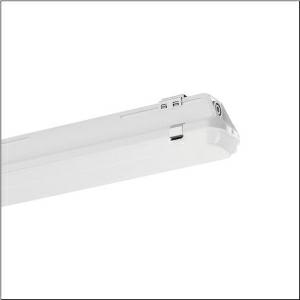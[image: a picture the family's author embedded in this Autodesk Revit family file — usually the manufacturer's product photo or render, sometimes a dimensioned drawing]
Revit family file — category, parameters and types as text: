
# Revit family: monsun_r__11_51fp208p460h_1e38
name_source: partatom
category: Lighting Fixtures
units: mm (PartAtom-declared; Revit-internal decimal feet)

## family parameters
Cut with Voids When Loaded = No
Host = Face
Light Source = No
Part Type = Normal
Room Calculation Point = No
Round Connector Dimension = Use Diameter
Shared = No

## types (1)
- Monsun® 11 (1 x LED, 5490 lm, 33.9 W, 4000K)
    Apparent Load = 34 VA
    CIE Flux Codes = 45 75 93 94 100
    Color Rendering = 80
    Color Temperature = 4000K
    Default Elevation = 1800 mm
    Description = Monsun® 11, damp-proof luminaire, chain hanger, primary optical cover: enclosure, of PC, light emission: direct distribution, primary light characteristic: symmetric, installation type: suspended mounting, surface-mounted, horizontal mounting, vertical mounting, LED, rated luminous flux: 5.490lm, luminous efficacy: 162lm/W, light colour: 840, colour temperature: 4000K, control gear: ON/OFF, with terminal, 3-pole, max. 2.5mm², mains connection: 220..240V, AC, 50/60Hz, rated input power: 34W, luminaire housing, of glass-fibre reinforced polyester, uncoated, bright grey, incl. chain hanger, length: 1.590mm, width: 90mm, height: 88mm, clip for enclosure, of stainless steel (V2A), ceiling mounting element, of stainless steel (V2A), chain hanger, of stainless steel (V2A), protection rating (complete): IP66, insulation class (complete): insulation class I (protective earthing), certification: CE, ENEC, VDE, UKCA, protection symbol: D, impact resistance: IK08, permissible operating ambient temperature: -35..+40°C, standard: EN 50419, EN 60598-2-1, no direct snow, no direct sun, no direct rain, for indoor or canopied outdoor use, corresponds to IFS (International Featured Standards) requirements for safety and quality in the food industry, contact your sales advisor before using the luminaires in applications with unclear chemical exposure, large temperature fluctuations or condensation-forming humidity, LABS conformity tested according to VDMA 24364:2018-05, packaging unit: 1 piece
    Height = 89 mm
    Lamp = 1 x LED
    Lamp Light Flux = 5490 lm
    Lamp Power = 33.9 W
    Lamp count = 1
    Length = 1590 mm
    Luminous efficacy = 162 lm/W
    Manufacturer = Siteco
    ModVariant = No
    Model = 51FP208P460H
    Mounting Place = Ceiling
    Mounting Type = Surface mounted
    Number of Poles = 1
    OnlyDefault = Yes
    Power Factor = 1
    Product Name = Monsun® 11
    Product group = damp-proof luminaire
    ProductGroupID = 300
    Protection Class = Protection class I
    Protection Degree = IP 66
    RLX_Detail_Level = 1
    RLX_Emergency_Light_Flux = 0 lm
    RLX_Emergency_Type = 0
    RLX_Emergency_Type_DB = No
    RlxData = <blob elided: 88741 chars, md5=bf3f0788>
    Socket = socket
    Standby Power = 0 W
    System Light Flux = 5490 lm
    System Power = 34 W
    Type Comments = Product without accessories
    Type Image = l_1349237.jpg
    URL = http://relux.com
    VarID = ---
    Voltage = 0 V
    Weight = 0.00 kg
    Width = 90 mm

## geometry (parser evidence)
native form markers: Blend x4, Sweep x14
no freeform markers — native parametric forms only
